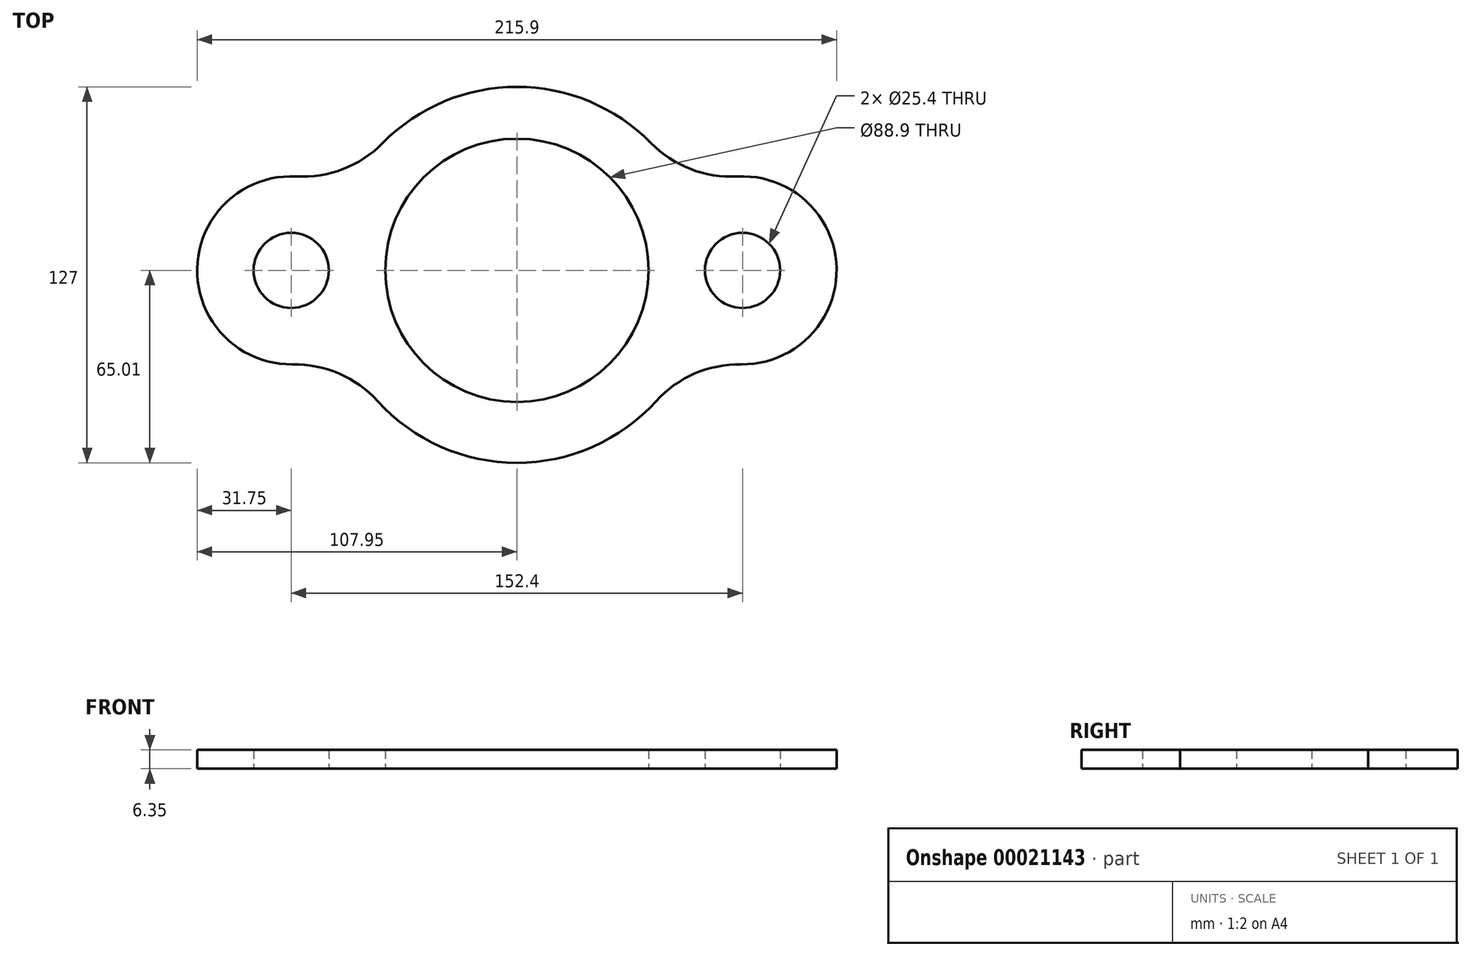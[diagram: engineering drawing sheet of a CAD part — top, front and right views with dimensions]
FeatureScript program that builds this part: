
annotation { "Feature Type Name" : "Feature", "Feature Type Description" : "" }
export const myFeature = defineFeature(function(context is Context, id is Id, definition is map)
    precondition{}
    {
        {
            var Q0;
            Q0=qCreatedBy(makeId("Top.planeOp"),FACE);
            var sketch = newSketch(context, id + "F0", { "sketchPlane" : qUnion([Q0])});
            skCircle(sketch, "E0", {"center": v(0, 0) * mm, "radius": 44.45 * mm});
            skCircle(sketch, "E1", {"center": v(-76.2, 0) * mm, "radius": 12.7 * mm});
            skCircle(sketch, "E2", {"center": v(76.2, 0) * mm, "radius": 12.7 * mm});
            skArc(sketch, "E3", {"start": v(75.74, -31.75) * mm, "mid": v(107.94, 0.63) * mm, "end": v(74.48, 31.7) * mm});
            skArc(sketch, "E4", {"start": v(-74.48, 31.7) * mm, "mid": v(-107.94, 0.63) * mm, "end": v(-75.74, -31.75) * mm});
            skArc(sketch, "E5", {"start": v(-47, -44.22) * mm, "mid": v(0, -65.01) * mm, "end": v(47, -44.22) * mm});
            skArc(sketch, "E6.trimOffspring", {"start": v(45.26, 43.02) * mm, "mid": v(0, 61.99) * mm, "end": v(-45.26, 43.02) * mm});
            skArc(sketch, "E7.filletArc", {"start": v(-74.48, 31.7) * mm, "mid": v(-58.65, 34.22) * mm, "end": v(-45.26, 43.02) * mm});
            skArc(sketch, "E8.filletArc", {"start": v(45.26, 43.02) * mm, "mid": v(58.65, 34.22) * mm, "end": v(74.48, 31.7) * mm});
            skArc(sketch, "E9.filletArc", {"start": v(-47, -44.22) * mm, "mid": v(-60.03, -34.9) * mm, "end": v(-75.74, -31.75) * mm});
            skArc(sketch, "E10.filletArc", {"start": v(75.74, -31.75) * mm, "mid": v(60.03, -34.9) * mm, "end": v(47, -44.22) * mm});
            skSolve(sketch);
        }
        {
            var Q0;
            Q0 = qSketchRegion(id + "F0", true);
            extrude(context, id + "F1", {"entities" : qUnion([Q0]), "depth" : 6.35 * mm});
        }
    });
